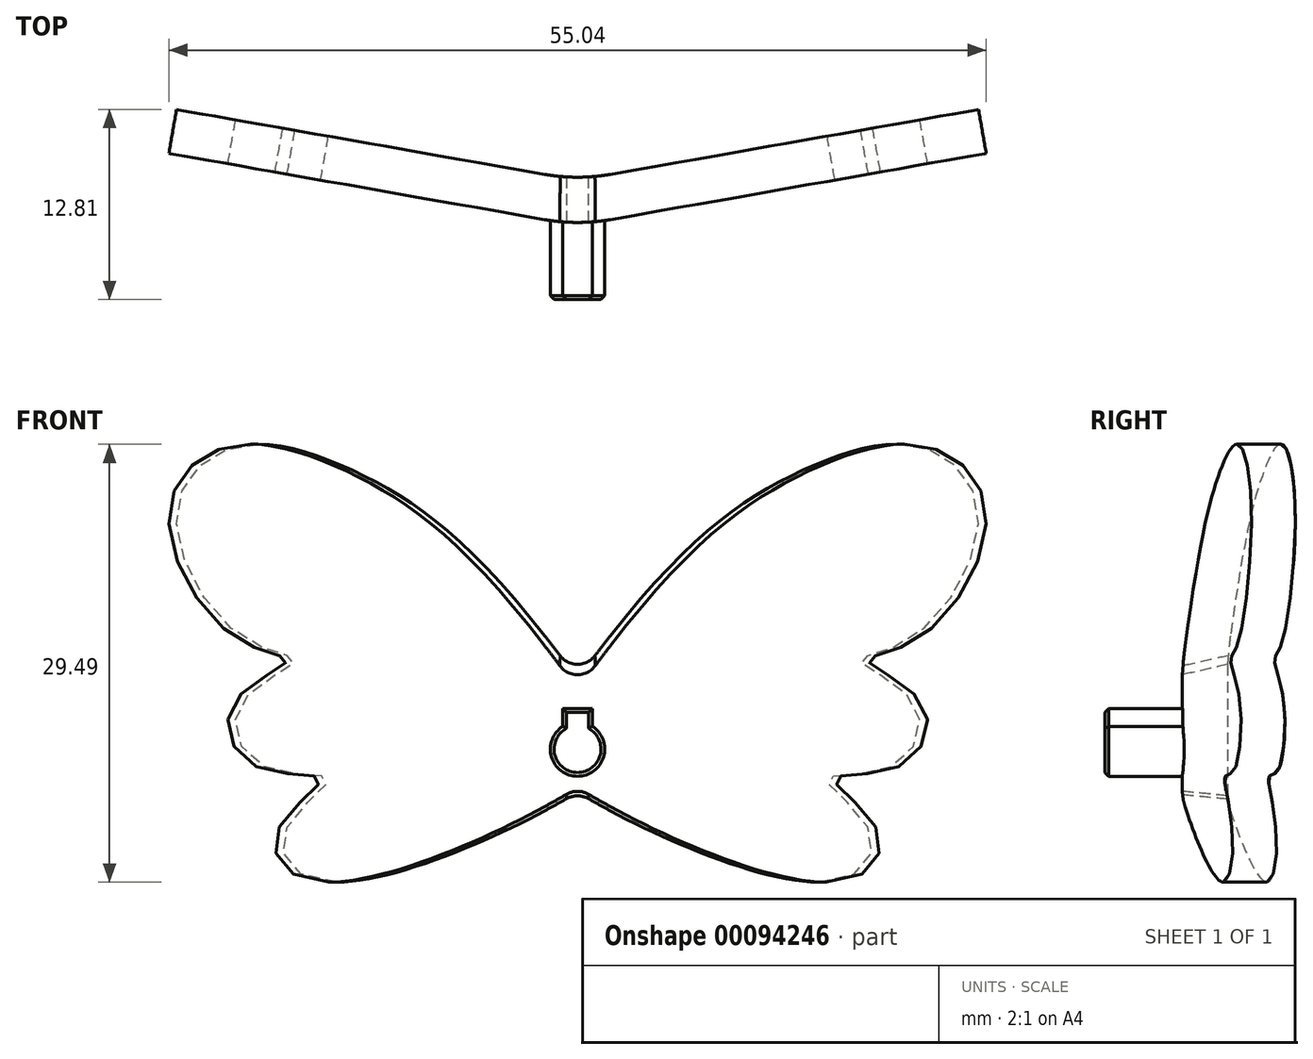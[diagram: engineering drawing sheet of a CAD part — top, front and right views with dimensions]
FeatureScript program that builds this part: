
annotation { "Feature Type Name" : "Feature", "Feature Type Description" : "" }
export const myFeature = defineFeature(function(context is Context, id is Id, definition is map)
    precondition{}
    {
        {
            var Q0;
            Q0=qCreatedBy(makeId("Front.planeOp"),FACE);
            var sketch = newSketch(context, id + "F0", { "sketchPlane" : qUnion([Q0])});
            skArc(sketch, "E0", {"start": v(-1, 1.54) * mm, "mid": v(0, -1.83) * mm, "end": v(1, 1.54) * mm});
            skLineSegment(sketch, "E1.top", {"start": v(0, 2.74) * mm, "end": v(-0.99, 2.74) * mm});
            skLineSegment(sketch, "E1.left", {"start": v(0, 0) * mm, "end": v(0, 2.74) * mm});
            skLineSegment(sketch, "E1.right", {"start": v(-0.99, 1.54) * mm, "end": v(-0.99, 2.74) * mm});
            skLineSegment(sketch, "E2.MirrorCS", {"start": v(0, 2.74) * mm, "end": v(0.99, 2.74) * mm});
            skLineSegment(sketch, "E3.MirrorCS", {"start": v(0.99, 1.54) * mm, "end": v(0.99, 2.74) * mm});
            skPoint(sketch, "E4.orphan", {"position": v(-0.99, 0) * mm});
            skPoint(sketch, "E5.orphan", {"position": v(0.99, 0) * mm});
            skSolve(sketch);
        }
        {
            var Q0;
            Q0=makeQuery(id+"F0.imprint","IMPRINT",FACE,{"disambiguationData":[TD([[makeQuery(id+"F0.imprint","IMPRINT",EDGE,{"derivedFrom":sQuery(id+"F0.wireOp",EDGE,"E0")}),1.0]])]});
            extrude(context, id + "F1", {"entities" : qUnion([Q0]), "depth" : 5 * mm, "hasSecondDirection" : true, "secondDirectionOppositeDirection" : true, "secondDirectionDepth" : 2 * mm});
        }
        {
            var Q0;
            Q0=qCreatedBy(makeId("Front.planeOp"),FACE);
            var sketch = newSketch(context, id + "F2", { "sketchPlane" : qUnion([Q0])});
            skLineSegment(sketch, "E6", {"start": v(0, 0) * mm, "end": v(0, 65) * mm, "construction": true});
            skSolve(sketch);
        }
        {
            var Q0;
            Q0=sQuery(id+"F2.wireOp",EDGE,"E6");
            cPlane(context, id + "F3", {"entities" : qUnion([Q0]), "cplaneType" : CPlaneType.LINE_ANGLE, "offset" : 152.4 * mm, "angle" : 80 * degree, "width" : 152.4 * mm, "height" : 152.4 * mm});
        }
        {
            var Q0;
            Q0=qCreatedBy(id+"F3.planeOp",FACE);
            var sketch = newSketch(context, id + "F4", { "sketchPlane" : qUnion([Q0])});
            skFitSpline(sketch, "E7", {"points": [v(0, -2.56) * mm, v(17.97, -8.89) * mm, v(20.53, -5.54) * mm, v(17.6, -2.04) * mm, v(21.96, -1.18) * mm, v(23.58, 3.01) * mm, v(19.9, 5.93) * mm, v(23.1, 7.35) * mm, v(27.94, 15.77) * mm, v(24.08, 20.32) * mm, v(15.56, 18.6) * mm, v(0, 3.97) * mm], "startDerivative": vector(68.75, -44.54) * mm, "endDerivative": vector(-131.41, -181.24) * mm});
            skLineSegment(sketch, "E8", {"start": v(0, 3.97) * mm, "end": v(0, -2.56) * mm});
            skLineSegment(sketch, "E9.bottom", {"start": v(27.94, 20.32) * mm, "end": v(-27.94, 20.32) * mm, "construction": true});
            skLineSegment(sketch, "E9.top", {"start": v(27.94, -8.89) * mm, "end": v(-27.94, -8.9) * mm, "construction": true});
            skLineSegment(sketch, "E9.left", {"start": v(27.94, 20.32) * mm, "end": v(27.94, -8.89) * mm, "construction": true});
            skLineSegment(sketch, "E9.right", {"start": v(-27.94, 20.32) * mm, "end": v(-27.94, -8.9) * mm, "construction": true});
            skSolve(sketch);
        }
        {
            var Q0;
            Q0=makeQuery(id+"F4.imprint","IMPRINT",FACE,{"disambiguationData":[TD([[makeQuery(id+"F4.imprint","IMPRINT",EDGE,{"derivedFrom":sQuery(id+"F4.wireOp",EDGE,"E7")}),1.0]])]});
            extrude(context, id + "F5", {"entities" : qUnion([Q0]), "depth" : 3 * mm});
        }
        {
            var Q0;
            Q0=makeQuery(id+"F5.opExtrude","SWEPT_BODY",BODY,{"disambiguationData":[OSD([sQuery(id+"F4.wireOp",EDGE,"E7"),sQuery(id+"F4.wireOp",EDGE,"E8")])]});
            var Q1;
            Q1=qCreatedBy(makeId("Right.planeOp"),FACE);
            mirror(context, id + "F6", {"operationType" : NewBodyOperationType.ADD, "entities" : qUnion([Q0]), "mirrorPlane" : qUnion([Q1])});
        }
        {
            var Q0;
            {var subQ0=makeQuery(id+"F5.opExtrude","SWEPT_FACE",FACE,{"disambiguationData":[OSD([sQuery(id+"F4.wireOp",EDGE,"E7")])]});Q0=makeQuery(id+"F6.boolean.opBoolean","INTERSECT",EDGE,{"disambiguationData":[OD(1.0)],"derivedFrom":[subQ0,makeQuery(id+"F6.opPattern","COPY",FACE,{"derivedFrom":subQ0,"instanceName":"1"})]});}
            var Q1;
            {var subQ0=makeQuery(id+"F5.opExtrude","SWEPT_FACE",FACE,{"disambiguationData":[OSD([sQuery(id+"F4.wireOp",EDGE,"E7")])]});Q1=makeQuery(id+"F6.boolean.opBoolean","INTERSECT",EDGE,{"disambiguationData":[OD(0.0)],"derivedFrom":[subQ0,makeQuery(id+"F6.opPattern","COPY",FACE,{"derivedFrom":subQ0,"instanceName":"1"})]});}
            fillet(context, id + "F7", {"entities" : qUnion([Q0, Q1]), "radius" : 1.5 * mm, "tangentPropagation" : true, "allowEdgeOverflow" : false});
        }
        {
            var Q0;
            {var subQ0=makeQuery(id+"F5.opExtrude","CAP_FACE",FACE,{"disambiguationData":[OSD([sQuery(id+"F4.wireOp",EDGE,"E7"),sQuery(id+"F4.wireOp",EDGE,"E8")])],"isStart":false});Q0=makeQuery(id+"F6.boolean.opBoolean","INTERSECT",EDGE,{"derivedFrom":[subQ0,makeQuery(id+"F6.opPattern","COPY",FACE,{"derivedFrom":subQ0,"instanceName":"1"})]});}
            var Q1;
            {var subQ0=makeQuery(id+"F5.opExtrude","CAP_EDGE",EDGE,{"disambiguationData":[OSD([sQuery(id+"F4.wireOp",EDGE,"E8")])],"isStart":true});Q1=makeQuery(id+"F6.boolean.opBoolean","MERGE",EDGE,{"disambiguationData":[OD(1.0)],"derivedFrom":[subQ0,makeQuery(id+"F6.opPattern","COPY",EDGE,{"derivedFrom":subQ0,"instanceName":"1"})]});}
            fillet(context, id + "F8", {"entities" : qUnion([Q0, Q1]), "radius" : 12.7 * mm, "tangentPropagation" : true, "allowEdgeOverflow" : false});
        }
        {
            var Q0;
            Q0=makeQuery(id+"F1.opExtrude","CAP_EDGE",EDGE,{"disambiguationData":[OSD([sQuery(id+"F0.wireOp",EDGE,"E1.top"),sQuery(id+"F0.wireOp",EDGE,"E2.MirrorCS")])],"isStart":false});
            var Q1;
            Q1=makeQuery(id+"F1.opExtrude","CAP_EDGE",EDGE,{"disambiguationData":[OSD([sQuery(id+"F0.wireOp",EDGE,"E1.right")])],"isStart":false});
            var Q2;
            Q2=makeQuery(id+"F1.opExtrude","CAP_EDGE",EDGE,{"disambiguationData":[OSD([sQuery(id+"F0.wireOp",EDGE,"E3.MirrorCS")])],"isStart":false});
            var Q3;
            Q3=makeQuery(id+"F1.opExtrude","CAP_EDGE",EDGE,{"disambiguationData":[OSD([sQuery(id+"F0.wireOp",EDGE,"E0")])],"isStart":false});
            chamfer(context, id + "F9", {"entities" : qUnion([Q0, Q1, Q2, Q3]), "width" : 0.25 * mm});
        }
    });
